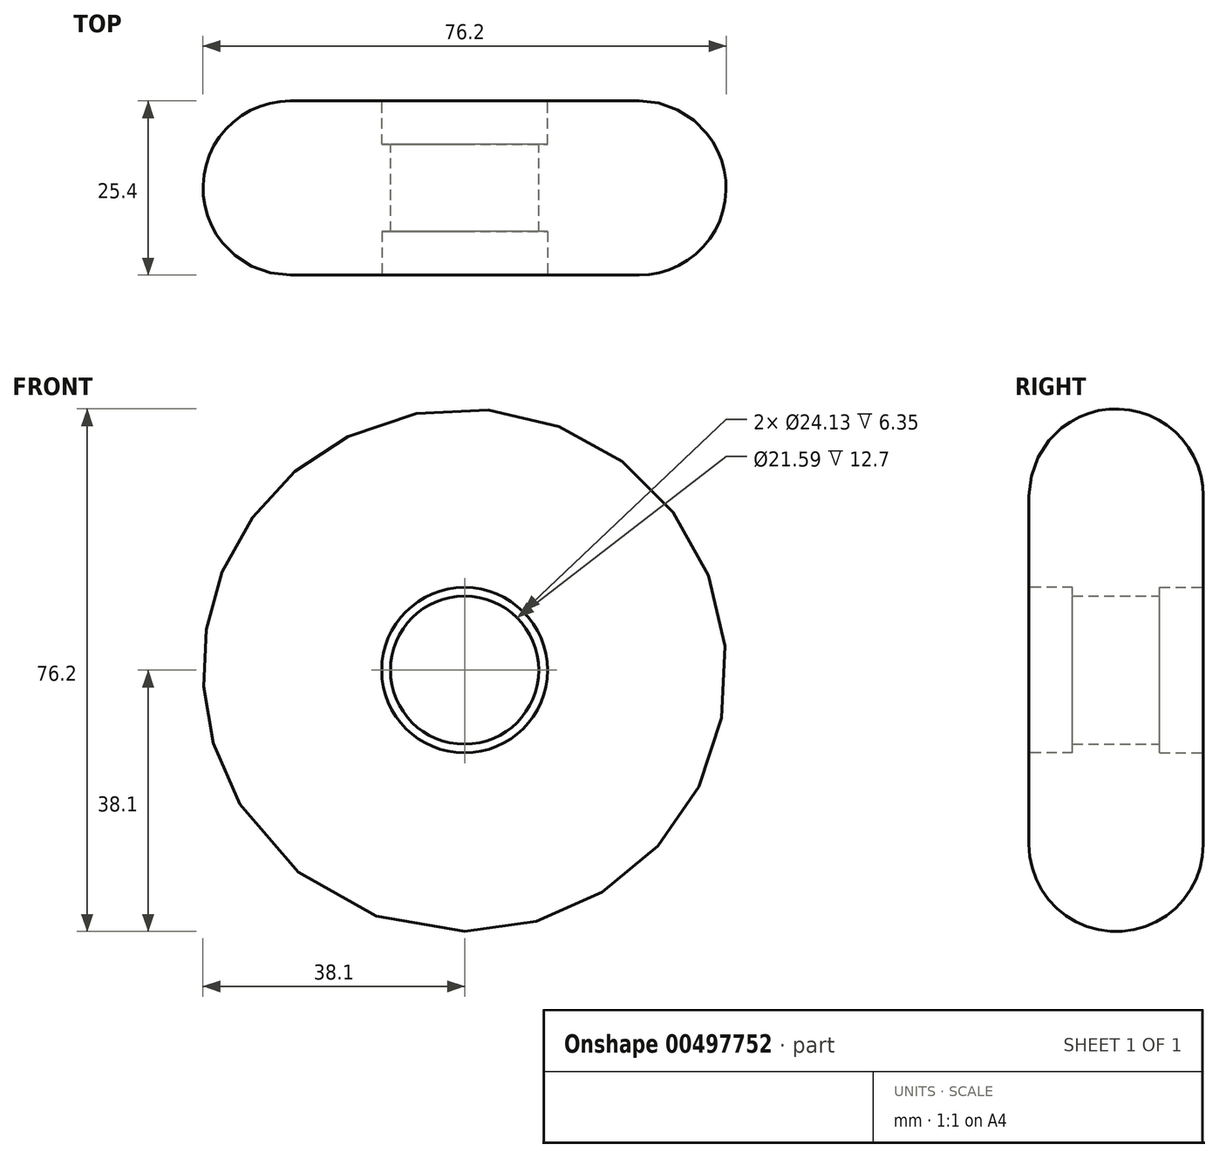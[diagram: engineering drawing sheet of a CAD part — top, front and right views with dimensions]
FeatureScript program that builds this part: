
annotation { "Feature Type Name" : "Feature", "Feature Type Description" : "" }
export const myFeature = defineFeature(function(context is Context, id is Id, definition is map)
    precondition{}
    {
        {
            var Q0;
            Q0=qCreatedBy(makeId("Front.planeOp"),FACE);
            var sketch = newSketch(context, id + "F0", { "sketchPlane" : qUnion([Q0])});
            skCircle(sketch, "E0", {"center": v(0, 0) * mm, "radius": 38.1 * mm});
            skSolve(sketch);
        }
        {
            var Q0;
            Q0=makeQuery(id+"F0.imprint","IMPRINT",FACE,{"disambiguationData":[TD([[makeQuery(id+"F0.imprint","IMPRINT",EDGE,{"derivedFrom":sQuery(id+"F0.wireOp",EDGE,"E0")}),1.0]])]});
            extrude(context, id + "F1", {"entities" : qUnion([Q0]), "depth" : 12.7 * mm});
        }
        {
            var Q0;
            Q0=makeQuery(id+"F1.opExtrude","CAP_EDGE",EDGE,{"disambiguationData":[OSD([sQuery(id+"F0.wireOp",EDGE,"E0")])],"isStart":false});
            fillet(context, id + "F2", {"entities" : qUnion([Q0]), "radius" : 12.7 * mm, "tangentPropagation" : true, "allowEdgeOverflow" : false});
        }
        {
            var Q0;
            Q0=qCreatedBy(makeId("Front.planeOp"),FACE);
            var sketch = newSketch(context, id + "F3", { "sketchPlane" : qUnion([Q0])});
            skCircle(sketch, "E1", {"center": v(0, 0) * mm, "radius": 10.8 * mm});
            skSolve(sketch);
        }
        {
            var Q0;
            Q0 = qSketchRegion(id + "F3", true);
            extrude(context, id + "F4", {"entities" : qUnion([Q0]), "operationType" : NewBodyOperationType.REMOVE, "depth" : 25.4 * mm});
        }
        {
            var Q0;
            Q0=qCreatedBy(makeId("Front.planeOp"),FACE);
            cPlane(context, id + "F5", {"entities" : qUnion([Q0]), "cplaneType" : CPlaneType.OFFSET, "offset" : 12.7 * mm, "width" : 152.4 * mm, "height" : 152.4 * mm});
        }
        {
            var Q0;
            Q0=qCreatedBy(id+"F5.planeOp",FACE);
            var sketch = newSketch(context, id + "F6", { "sketchPlane" : qUnion([Q0])});
            skCircle(sketch, "E2", {"center": v(0, 0) * mm, "radius": 12.06 * mm});
            skSolve(sketch);
        }
        {
            var Q0;
            Q0=makeQuery(id+"F6.imprint","IMPRINT",FACE,{"disambiguationData":[TD([[makeQuery(id+"F6.imprint","IMPRINT",EDGE,{"derivedFrom":sQuery(id+"F6.wireOp",EDGE,"E2")}),1.0]])]});
            extrude(context, id + "F7", {"entities" : qUnion([Q0]), "operationType" : NewBodyOperationType.REMOVE, "oppositeDirection" : true, "depth" : 6.35 * mm});
        }
        {
            var Q0;
            Q0=makeQuery(id+"F1.opExtrude","SWEPT_BODY",BODY,{"disambiguationData":[OSD([sQuery(id+"F0.wireOp",EDGE,"E0")])]});
            var Q1;
            Q1=qCreatedBy(makeId("Front.planeOp"),FACE);
            mirror(context, id + "F8", {"operationType" : NewBodyOperationType.ADD, "entities" : qUnion([Q0]), "mirrorPlane" : qUnion([Q1])});
        }
    });
